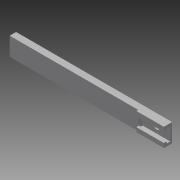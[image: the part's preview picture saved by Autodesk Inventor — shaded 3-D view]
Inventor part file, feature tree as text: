
AUTODESK INVENTOR PART (.ipt)
format: ipt  version: 2013 (Build 170138000, 138)  size: 157,184 bytes
history: native  units: in
note: dims shown in document units (in); Inventor stores cm internally (conversion verified against a paired STEP export)
features: extrude x8, sketch x7
ambient origin geometry x8: Origin, YZ Plane, XZ Plane, XY Plane, X Axis, Y Axis, Z Axis, Center Point
bodies: Solid1 (feature_tree)
feature tree (15):
  extrude  "Extrusion1"  Depth=1.0in
  extrude  "Extrusion2"  Depth=1.5in
  extrude  "Extrusion3"  Depth=0.365in
  extrude  "Extrusion4"  Depth=0.35in TaperAngle=0.0deg
  extrude  "Extrusion5"  Depth=0.1in TaperAngle=0.0deg
  sketch  "Sketch6"  dims[d14=0.2in d15=0.1in d16=0.0in]
  extrude  "Extrusion6"  Depth=0.1in TaperAngle=0.0deg
  extrude  "Extrusion7"  Depth=0.1in TaperAngle=0.0deg
  extrude  "Extrusion8"  Depth=0.1in TaperAngle=0.0deg
  sketch  "Sketch1"  dims[d0=8.5in d1=1.0in]
  sketch  "Sketch2"  dims[d2=0.35in d3=0.0in d4=1.5in]
  sketch  "Sketch3"  dims[d5=0.365in d6=0.365in]
  sketch  "Sketch4"  dims[d7=0.35in d8=0.0in d9=0.35in d10=0.0in]
  sketch  "Sketch5"  dims[d11=0.2in d12=0.1in d13=0.0in]
  sketch  "Sketch7"  dims[d19=0.15in d20=0.1in d21=0.0in d22=0.1in d23=0.0in d24=1.5in d25=0.35in d26=0.1in d27=0.0in]
